# Revit family: Resideo_VC-ValveBody_VCZAsss
name_source: partatom
category: Pipe Fittings
units: mm (PartAtom-declared; Revit-internal decimal feet)

## family parameters
Always vertical = Yes
Cut with Voids When Loaded = No
OmniClass Number = 23.65.55.14
OmniClass Title = Valves for Liquid Services
Part Type = Transition
Round Connector Dimension = Use Diameter
Shared = No
Work Plane-Based = No

## types (8) — shared parameters
Assembly Code = D20
AssetType = Fixed
BIMObjectName = Resideo_VC-ValveBody_VCZA
ClassificationName = Uniclass2015
ClassificationValue = Pr_65_54
Description = BODY VALVE
DocumentationCertificates = https://www.bimstore.co
DocumentationInstallationGuide = https://www.bimstore.co
DocumentationLiterature = https://www.bimstore.co
DocumentationMaintenance = https://www.bimstore.co
DocumentationTechnical = https://www.bimstore.co
DurationUnit = Year
IfcExportAs = IfcValve
IfcExportType = IfcValveTypeEnum.REGULATING
Keynote = S
Manufacturer = Resideo
ManufacturerName = Resideo
Material = Brass
MaximumDifferentialPressure = 4.0 bar
MaximumMediaTemperature = 95°C
MediumType = Water or water-glycol mixture according to VDI 2035
MinimumMediaTemperature = 1°C
ModelReference = BODY VALVE
NBSDescription = Valve products
NBSObjectName = Resideo - Valve products
NominalDepth = 47 mm  [stored 0.154199 ft]
NominalLength = 94 mm  [stored 0.308399 ft]
NominalPressure = PN20
PrimaryMaterial = Resideo - Brass
ProductSeries = VC-A-int
ProductionYear = 2022
SecondaryMaterial = Resideo - Stainless Steel
Size = 50mm (D) x 93mm (H) x 65mm (L)
Type Comments = BODY VALVE
URL = https://www.resideo.com
WarrantyDurationLabor = 0
WarrantyDurationParts = 0
WarrantyDurationUnit = Year
WarrantyGuarantorLabor = https://www.resideo.com
WarrantyGuarantorParts = https://www.resideo.com
_BSBibleVersion = 16
_CurrentRevision = 1
_DistributedBy = https://www.bimstore.co
_ObjectUserGuide = https://www.bimstore.co
zero-valued in all types: Cost, Default Elevation, ExpectedLife, _BimSpecGuid

## per-type parameters (varying)
| type | ActuatorOffset | ConnectionDia | ConnectionRadius | ConnectionSize | ControlCharacteristics | FlowCapacity(A-B) | NominalHeight | SpareParts | VCZAH1100/U | VCZAJ1000/U | VCZAJ1100/U | VCZAP1100/U | Weight | a | b | c | d | e |
| VCZAH1100 | 39.5 mm | 20 mm  [stored 0.0656168 ft] | 10 mm  [stored 0.0328084 ft] | 3/4" | Modulating | 4.5 m³/h | 83 mm  [stored 0.27231 ft] | VC Series replacement cartridge for 2-port zone valves, on/off [VCZZ1000/U] | Yes | No | No | No | 0.51 kg | 19.5 mm | 39.5 mm | 55.7 mm | 26.7 mm | 4 mm  [stored 0.0131234 ft] |
| VCZAJ1000 | 39.5 mm | 20 mm  [stored 0.0656168 ft] | 10 mm  [stored 0.0328084 ft] | 3/4" | On/Off | 5.0 m³/h | 83 mm  [stored 0.27231 ft] | VC Series replacement cartridge for 2-port zone valves, on/off [VCZZ1000/U] | No | Yes | No | No | 0.54 kg | 19.5 mm | 39.5 mm | 55.7 mm | 26.7 mm | 4 mm  [stored 0.0131234 ft] |
| VCZAJ1100 | 39.5 mm | 20 mm  [stored 0.0656168 ft] | 10 mm  [stored 0.0328084 ft] | 3/4" | Modulating | 4.5 m³/h | 83 mm  [stored 0.27231 ft] | VC Series replacement cartridge for 2-port zone valves, on/off [VCZZ1100/U] | No | No | Yes | No | 0.54 kg | 19.5 mm | 39.5 mm | 55.7 mm | 26.7 mm | 4 mm  [stored 0.0131234 ft] |
| VCZAP1100 | 38 mm  [stored 0.124672 ft] | 25 mm  [stored 0.082021 ft] | 12.5 mm  [stored 0.0410105 ft] | 1" | Modulating | 5.7 m³/h | 82 mm  [stored 0.269029 ft] | VC Series replacement cartridge for 2-port zone valves, on/off [VCZZ1100/U] | No | No | No | Yes | 0.57 kg | 21 mm  [stored 0.0688976 ft] | 38 mm  [stored 0.124672 ft] | 53.1 mm  [stored 0.174213 ft] | 25.2 mm  [stored 0.0826772 ft] | 3.8 mm |
| VCZAP1000 | 38 mm  [stored 0.124672 ft] | 25 mm  [stored 0.082021 ft] | 12.5 mm  [stored 0.0410105 ft] | 1" | On/Off | 5.5 m³/h | 82 mm  [stored 0.269029 ft] | VC Series replacement cartridge for 2-port zone valves, on/off [VCZZ1000/U] | No | No | No | Yes | 0.57 kg | 21 mm  [stored 0.0688976 ft] | 38 mm  [stored 0.124672 ft] | 53.1 mm  [stored 0.174213 ft] | 25.2 mm  [stored 0.0826772 ft] | 3.8 mm |
| VCZAH1000 | 39.5 mm | 20 mm  [stored 0.0656168 ft] | 10 mm  [stored 0.0328084 ft] | 3/4" | On/Off | 5.3 m³/h | 83 mm  [stored 0.27231 ft] | VC Series replacement cartridge for 2-port zone valves, on/off [VCZZ1000/U] | Yes | No | No | No | 0.51 kg | 19.5 mm | 39.5 mm | 55.7 mm | 26.7 mm | 4 mm  [stored 0.0131234 ft] |
| VCZAQ1100 | 38 mm  [stored 0.124672 ft] | 25 mm  [stored 0.082021 ft] | 12.5 mm  [stored 0.0410105 ft] | 1" | Modulating | 5.3 m³/h | 82 mm  [stored 0.269029 ft] | VC Series replacement cartridge for 2-port zone valves, on/off [VCZZ1100/U] | No | No | No | Yes | 0.53 kg | 21 mm  [stored 0.0688976 ft] | 38 mm  [stored 0.124672 ft] | 53.1 mm  [stored 0.174213 ft] | 25.2 mm  [stored 0.0826772 ft] | 3.8 mm |
| VCZAQ1000 | 38 mm  [stored 0.124672 ft] | 25 mm  [stored 0.082021 ft] | 12.5 mm  [stored 0.0410105 ft] | 1" | On/Off | 5.5 m³/h | 82 mm  [stored 0.269029 ft] | VC Series replacement cartridge for 2-port zone valves, on/off [VCZZ1000/U] | No | No | No | Yes | 0.53 kg | 21 mm  [stored 0.0688976 ft] | 38 mm  [stored 0.124672 ft] | 53.1 mm  [stored 0.174213 ft] | 25.2 mm  [stored 0.0826772 ft] | 3.8 mm |

note: column(s) folded — value = type name in every type: Model, ModelNumber, TypeName

note: [stored X ft] marks values corroborated as IEEE doubles in the binary element streams (Revit-internal decimal feet)

## geometry (parser evidence)
native form markers: Sweep x1
no freeform markers — native parametric forms only
